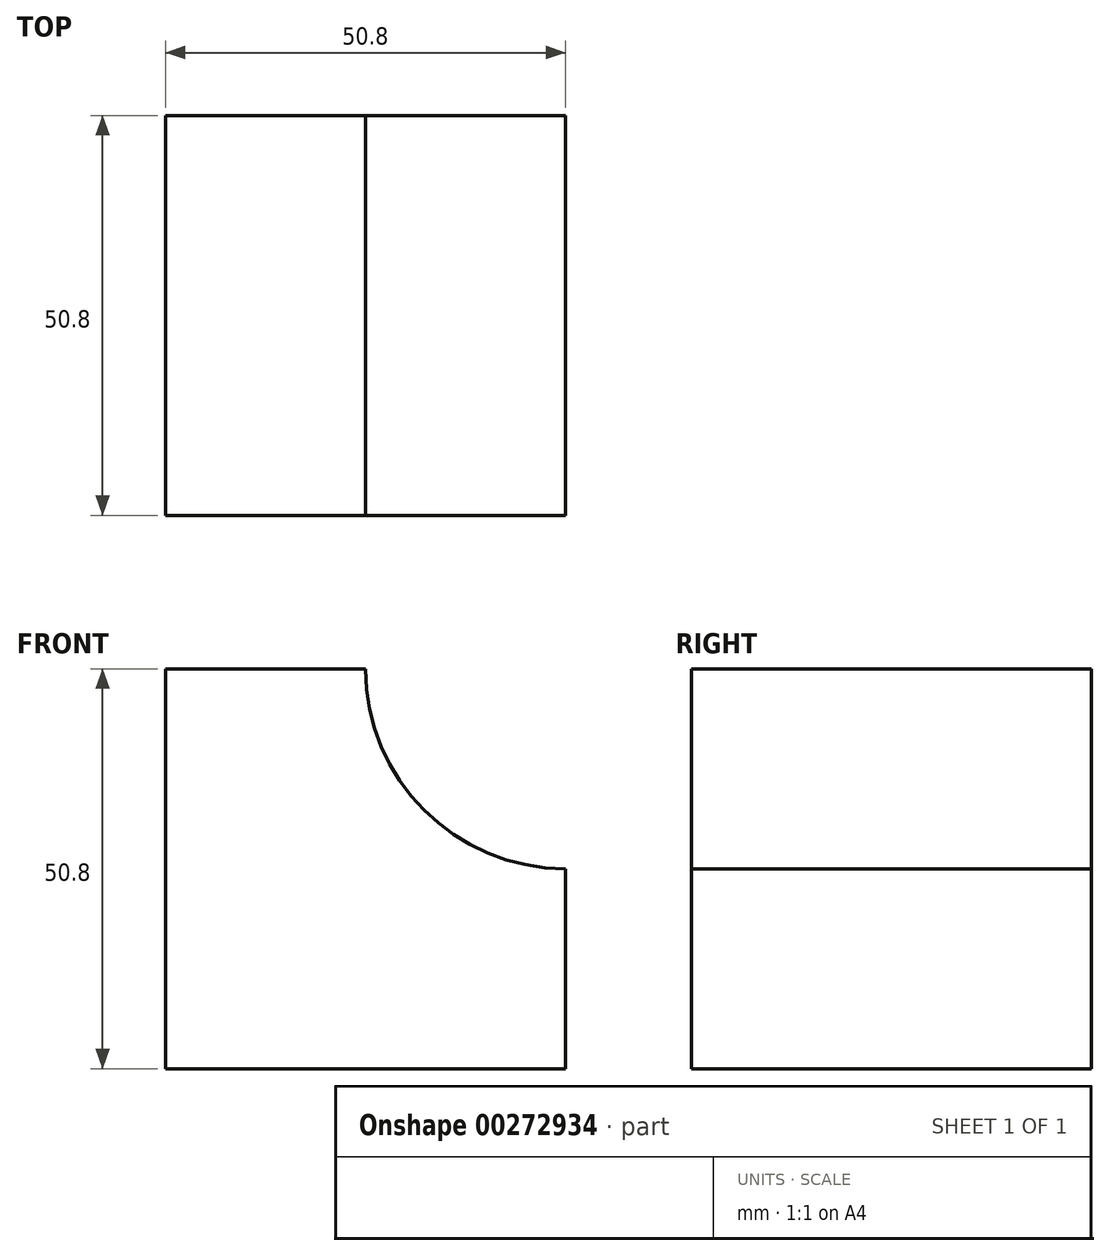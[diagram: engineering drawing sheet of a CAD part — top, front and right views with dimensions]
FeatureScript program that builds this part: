
annotation { "Feature Type Name" : "Feature", "Feature Type Description" : "" }
export const myFeature = defineFeature(function(context is Context, id is Id, definition is map)
    precondition{}
    {
        {
            var Q0;
            Q0=qCreatedBy(makeId("Front.planeOp"),FACE);
            var sketch = newSketch(context, id + "F0", { "sketchPlane" : qUnion([Q0])});
            skLineSegment(sketch, "E0", {"start": v(-41.44, 25.4) * mm, "end": v(-41.44, -25.4) * mm});
            skLineSegment(sketch, "E1", {"start": v(-41.44, -25.4) * mm, "end": v(9.36, -25.4) * mm});
            skLineSegment(sketch, "E2", {"start": v(9.36, -25.4) * mm, "end": v(9.36, 0) * mm});
            skLineSegment(sketch, "E3", {"start": v(-16.04, 25.4) * mm, "end": v(-41.44, 25.4) * mm});
            skArc(sketch, "E4", {"start": v(-16.04, 25.4) * mm, "mid": v(-8.6, 7.44) * mm, "end": v(9.36, 0) * mm});
            skSolve(sketch);
        }
        {
            var Q0;
            Q0 = qSketchRegion(id + "F0", true);
            extrude(context, id + "F1", {"entities" : qUnion([Q0]), "depth" : 50.8 * mm});
        }
    });
